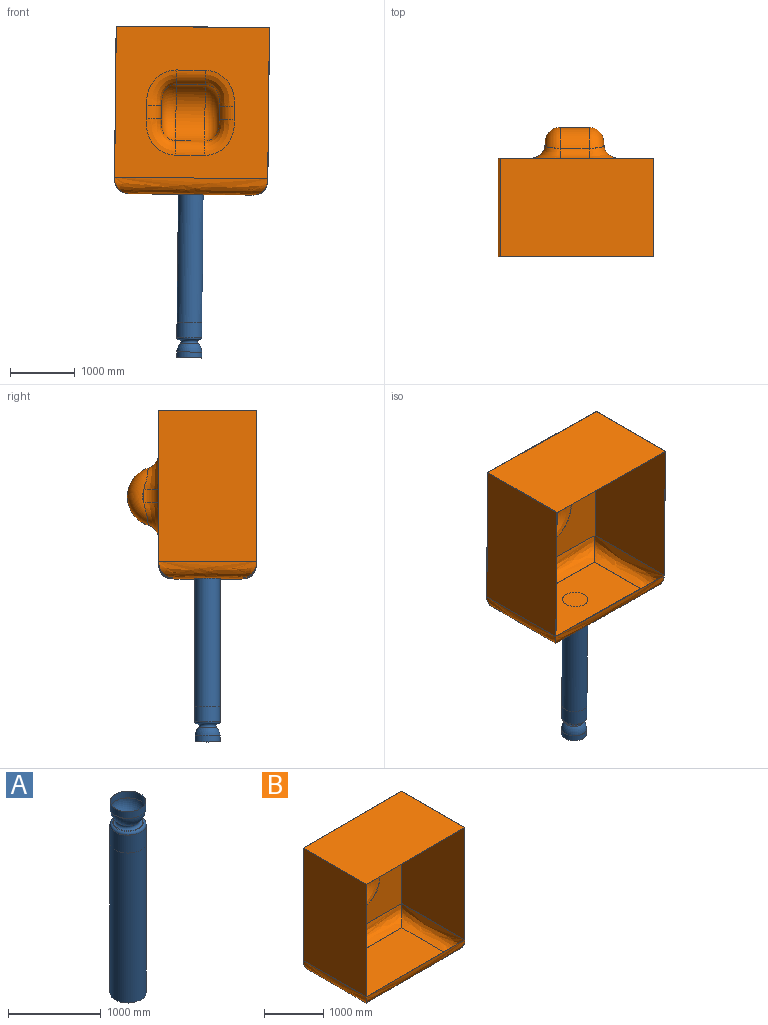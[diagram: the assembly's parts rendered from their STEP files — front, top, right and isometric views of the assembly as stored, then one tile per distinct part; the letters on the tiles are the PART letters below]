
ASSEMBLY  parts=2 mates=1
PART A: 15 faces, bbox 420.5x420.5x2522.8 mm
  f0: cylinder r=192.69mm len=385.39mm, axis (0,0,-1), area 109724.3mm2, adj f1,f2
  f1: plane 385.39x385.39mm, normal (0,0,1), area 3055mm2, adj f0,f7
  f2: torus R=4.5mm, axis (0,0,1), area 164781.4mm2, adj f0,f6
  f3: cylinder r=194.25mm len=2213.47mm, axis (0,0,1), area 2701505.7mm2, adj f5,f14
  f4: plane 327.53x327.53mm, normal (0,0,1), area 7825.1mm2, adj f5,f6
  f5: torus R=163.77mm, axis (0,0,1), area 55102.3mm2, adj f3,f4
  f6: torus R=155.98mm, axis (0,0,1), area 60937.7mm2, adj f2,f4
  f7: cylinder r=190.15mm len=380.31mm, axis (0,0,-1), area 108278mm2, adj f1,f8
  f8: torus R=4.5mm, axis (0,0,1), area 160420.5mm2, adj f7,f13
  f9: cylinder r=191.71mm len=383.41mm, axis (0,0,1), area 285984.3mm2, adj f10,f12
  f10: plane 383.41x383.41mm, normal (0,0,1), area 115457.2mm2, adj f9
  f11: plane 327.53x327.53mm, normal (0,0,-1), area 7825.1mm2, adj f12,f13
  f12: torus R=163.77mm, axis (0,0,1), area 50064.5mm2, adj f9,f11
  f13: torus R=155.98mm, axis (0,0,1), area 65108.8mm2, adj f8,f11
  f14: plane 388.49x388.49mm, normal (0,0,-1), area 118537mm2, adj f3
PART B: 46 faces, bbox 2609.5x2111.9x2591.7 mm
  f0: plane 2367.69x2332.65mm, normal (0,-1,0), area 17850.9mm2, adj f1,f2,f4,f8,f24,f25,f27
  f1: plane 2332.65x1512.67mm, normal (-1,0,0), area 3528526.1mm2, adj f0,f4,f5,f6
  f2: plane 2332.65x1512.67mm, normal (1,0,0), area 3528526.1mm2, adj f0,f4,f5,f9
  f3: plane 1859.69x1004.67mm, normal (0,0,-1), area 1868372.7mm2, adj f6,f7,f8,f9
  f4: plane 2367.69x1512.67mm, normal (0,0,1), area 3581531.9mm2, adj f0,f1,f2,f5
  f5: plane 2367.69x2332.65mm, normal (0,1,0), area 3927596mm2, adj f1,f2,f4,f7,f13,f14,f15,f17
  f6: bspline ~1663.93x254mm, area 552141.9mm2, adj f1,f3,f7,f8
  f7: bspline ~2604.46x254mm, area 904668.6mm2, adj f3,f5,f6,f9
  f8: bspline ~2604.46x254mm, area 904668.6mm2, adj f0,f3,f6,f9,f23
  f9: bspline ~1663.93x254mm, area 552141.9mm2, adj f2,f3,f7,f8
  f10: cylinder r=460.8mm len=878.29mm, axis (-1,0,0), area 520510mm2, adj f13,f16,f18,f21
  f11: plane 202.95x23.35mm, normal (1,0,0), area 3192.2mm2, adj f20,f21
  f12: plane 202.95x23.35mm, normal (-1,0,0), area 3192.2mm2, adj f15,f16
  f13: cylinder r=228.6mm len=447.18mm, axis (-1,0,0), area 129110.9mm2, adj f5,f10,f14,f22
  f14: bspline ~584x475.83mm, area 186977mm2, adj f5,f13,f15,f16
  f15: cylinder r=228.6mm len=228.6mm, axis (0,0,-1), area 72877.1mm2, adj f5,f12,f14,f17
  f16: torus R=232.2mm, axis (1,0,0), area 309094.1mm2, adj f10,f12,f14,f17
  f17: bspline ~573.32x481.77mm, area 186969.6mm2, adj f5,f15,f16,f18
  f18: cylinder r=228.6mm len=447.18mm, axis (-1,0,0), area 129110.9mm2, adj f5,f10,f17,f19
  f19: bspline ~584x475.83mm, area 186977mm2, adj f5,f18,f20,f21
  f20: cylinder r=228.6mm len=228.6mm, axis (0,0,1), area 72877.1mm2, adj f5,f11,f19,f22
  f21: torus R=232.2mm, axis (1,0,0), area 309089.5mm2, adj f10,f11,f19,f22
  f22: bspline ~573.32x481.77mm, area 186969.6mm2, adj f5,f13,f20,f21
  f23: bspline ~2367.69x2.54mm, area 6001mm2, adj f8,f24,f25,f31
  f24: plane 2330.11x1510.13mm, normal (1,0,0), area 3518765.4mm2, adj f0,f23,f27,f28,f29
  f25: plane 2330.11x1510.13mm, normal (-1,0,0), area 3518765.4mm2, adj f0,f23,f27,f28,f32
  f26: plane 1859.69x1004.67mm, normal (0,0,1), area 1868372.7mm2, adj f29,f30,f31,f32
  f27: plane 2362.61x1510.13mm, normal (0,0,-1), area 3567846.5mm2, adj f0,f24,f25,f28
  f28: plane 2362.61x2330.11mm, normal (0,-1,0), area 3909745.1mm2, adj f24,f25,f27,f30,f36,f37,f38,f40
  f29: offset ~1669.01x259.08mm, area 545470.7mm2, adj f24,f26,f30,f31
  f30: offset ~2609.54x259.08mm, area 894585.9mm2, adj f26,f28,f29,f32
  f31: offset ~2609.54x259.08mm, area 894585.9mm2, adj f23,f26,f29,f32
  f32: offset ~1669.01x259.08mm, area 545470.7mm2, adj f25,f26,f30,f31
  f33: cylinder r=458.26mm len=873.45mm, axis (-1,0,0), area 517640.9mm2, adj f36,f39,f41,f44
  f34: plane 202.95x23.35mm, normal (-1,0,0), area 3192.2mm2, adj f43,f44
  f35: plane 202.95x23.35mm, normal (1,0,0), area 3192.2mm2, adj f38,f39
  f36: cylinder r=231.14mm len=447.18mm, axis (-1,0,0), area 130545.5mm2, adj f28,f33,f37,f45
  f37: bspline ~584x475.83mm, area 188354.7mm2, adj f28,f36,f38,f39
  f38: cylinder r=231.14mm len=231.14mm, axis (0,0,-1), area 73686.9mm2, adj f28,f35,f37,f40
  f39: torus R=232.2mm, axis (1,0,0), area 304291mm2, adj f33,f35,f37,f40
  f40: bspline ~573.32x481.77mm, area 188347.4mm2, adj f28,f38,f39,f41
  f41: cylinder r=231.14mm len=447.18mm, axis (-1,0,0), area 130545.5mm2, adj f28,f33,f40,f42
  f42: bspline ~584x475.83mm, area 188354.7mm2, adj f28,f41,f43,f44
  f43: cylinder r=231.14mm len=231.14mm, axis (0,0,1), area 73686.9mm2, adj f28,f34,f42,f45
  f44: torus R=232.2mm, axis (1,0,0), area 304286.5mm2, adj f33,f34,f42,f45
  f45: bspline ~573.32x481.77mm, area 188347.4mm2, adj f28,f36,f43,f44
PLACE A rot(axis=(0,-1,0),179.4deg) t=(1069.55,1850.59,-1104.35)mm
PLACE B rot(axis=(0,1,0),0.6deg) t=(1094.02,1578.59,1139.47)mm
MATE fastened B.f3 <-> A.f0  axis (-0.01,0,-1) through (1094.02,1850.59,1139.47)mm
